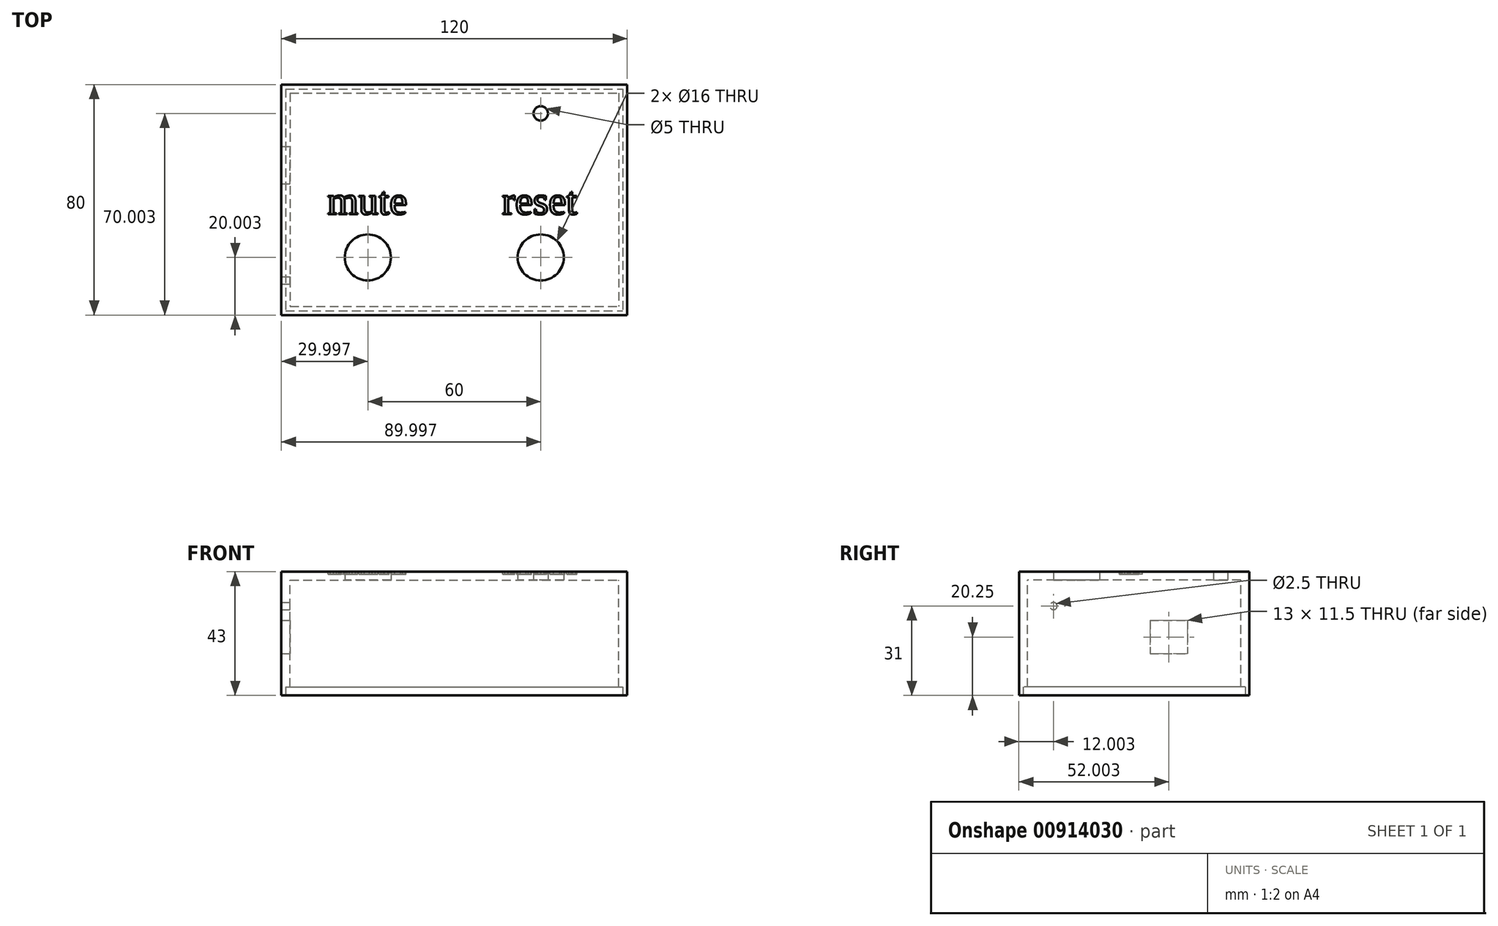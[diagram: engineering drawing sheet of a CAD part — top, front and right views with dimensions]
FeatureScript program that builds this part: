
annotation { "Feature Type Name" : "Feature", "Feature Type Description" : "" }
export const myFeature = defineFeature(function(context is Context, id is Id, definition is map)
    precondition{}
    {
        {
            var Q0;
            Q0=qCreatedBy(makeId("Top.planeOp"),FACE);
            var sketch = newSketch(context, id + "F0", { "sketchPlane" : qUnion([Q0])});
            skLineSegment(sketch, "E0.bottom", {"start": v(-70.32, 62.2) * mm, "end": v(49.68, 62.2) * mm});
            skLineSegment(sketch, "E0.top", {"start": v(-70.32, -17.8) * mm, "end": v(49.68, -17.8) * mm});
            skLineSegment(sketch, "E0.left", {"start": v(-70.32, 62.2) * mm, "end": v(-70.32, -17.8) * mm});
            skLineSegment(sketch, "E0.right", {"start": v(49.68, 62.2) * mm, "end": v(49.68, -17.8) * mm});
            skLineSegment(sketch, "E1", {"start": v(-10.32, 62.2) * mm, "end": v(-10.32, -17.8) * mm});
            skLineSegment(sketch, "E2", {"start": v(-70.32, 22.2) * mm, "end": v(49.68, 22.2) * mm});
            skLineSegment(sketch, "E3", {"start": v(19.68, 62.2) * mm, "end": v(19.68, -17.8) * mm});
            skLineSegment(sketch, "E4", {"start": v(-40.32, 62.2) * mm, "end": v(-40.32, -17.8) * mm});
            skLineSegment(sketch, "E5", {"start": v(-70.32, 52.2) * mm, "end": v(49.68, 52.2) * mm});
            skLineSegment(sketch, "E6", {"start": v(49.68, 2.2) * mm, "end": v(-70.32, 2.2) * mm});
            skCircle(sketch, "E7", {"center": v(19.68, 52.2) * mm, "radius": 2.5 * mm});
            skCircle(sketch, "E8", {"center": v(19.68, 2.2) * mm, "radius": 8 * mm});
            skCircle(sketch, "E9", {"center": v(-40.32, 2.2) * mm, "radius": 8 * mm});
            skSolve(sketch);
        }
        {
            var Q0;
            Q0 = qSketchRegion(id + "F0", true);
            var Q1;
            {var subQ0=sQuery(id+"F0.wireOp",EDGE,"E5");var subQ1=sQuery(id+"F0.wireOp",EDGE,"E1");var subQ2=makeQuery(id+"F0.imprint","INTERSECT",VERTEX,{"derivedFrom":[subQ1,subQ0]});Q1=makeQuery(id+"F0.imprint","IMPRINT",FACE,{"disambiguationData":[TD([[makeQuery(id+"F0.imprint","IMPRINT",EDGE,{"disambiguationData":[TD([[subQ2,-1.0]])],"derivedFrom":subQ1}),-1.0]])]});}
            var Q2;
            {var subQ0=sQuery(id+"F0.wireOp",EDGE,"E5");var subQ1=sQuery(id+"F0.wireOp",EDGE,"E1");var subQ2=makeQuery(id+"F0.imprint","INTERSECT",VERTEX,{"derivedFrom":[subQ1,subQ0]});Q2=makeQuery(id+"F0.imprint","IMPRINT",FACE,{"disambiguationData":[TD([[makeQuery(id+"F0.imprint","IMPRINT",EDGE,{"disambiguationData":[TD([[subQ2,-1.0]])],"derivedFrom":subQ1}),1.0]])]});}
            var Q3;
            {var subQ1=sQuery(id+"F0.wireOp",EDGE,"E1");var subQ5=sQuery(id+"F0.wireOp",EDGE,"E2");var subQ6=makeQuery(id+"F0.imprint","INTERSECT",VERTEX,{"derivedFrom":[subQ1,subQ5]});Q3=makeQuery(id+"F0.imprint","IMPRINT",FACE,{"disambiguationData":[TD([[makeQuery(id+"F0.imprint","IMPRINT",EDGE,{"disambiguationData":[TD([[subQ6,-1.0]])],"derivedFrom":subQ1}),1.0]])]});}
            var Q4;
            {var subQ1=sQuery(id+"F0.wireOp",EDGE,"E2");var subQ5=sQuery(id+"F0.wireOp",EDGE,"E1");var subQ6=makeQuery(id+"F0.imprint","INTERSECT",VERTEX,{"derivedFrom":[subQ5,subQ1]});Q4=makeQuery(id+"F0.imprint","IMPRINT",FACE,{"disambiguationData":[TD([[makeQuery(id+"F0.imprint","IMPRINT",EDGE,{"disambiguationData":[TD([[subQ6,-1.0]])],"derivedFrom":subQ5}),-1.0]])]});}
            extrude(context, id + "F1", {"entities" : qUnion([Q0, Q1, Q2, Q3, Q4]), "depth" : 3 * mm, "offsetDistance" : 25 * mm});
        }
        {
            var Q0;
            {var subQ1=sQuery(id+"F0.wireOp",EDGE,"E0.top");var subQ5=sQuery(id+"F0.wireOp",EDGE,"E0.left");var subQ6=makeQuery(id+"F0.imprint","INTERSECT",VERTEX,{"derivedFrom":[subQ1,subQ5]});Q0=makeQuery(id+"F0.imprint","IMPRINT",FACE,{"disambiguationData":[TD([[makeQuery(id+"F0.imprint","IMPRINT",EDGE,{"disambiguationData":[TD([[subQ6,-1.0]])],"derivedFrom":subQ1}),1.0]])]});}
            var sketch = newSketch(context, id + "F2", { "sketchPlane" : qUnion([Q0])});
            skLineSegment(sketch, "E10.0", {"start": v(-67.32, -14.8) * mm, "end": v(46.68, -14.8) * mm});
            skLineSegment(sketch, "E10.1", {"start": v(-67.32, 59.2) * mm, "end": v(-67.32, -14.8) * mm});
            skLineSegment(sketch, "E10.2", {"start": v(-67.32, 59.2) * mm, "end": v(46.68, 59.2) * mm});
            skLineSegment(sketch, "E10.3", {"start": v(46.68, 59.2) * mm, "end": v(46.68, -14.8) * mm});
            skLineSegment(sketch, "E11.0", {"start": v(-70.32, -17.8) * mm, "end": v(49.68, -17.8) * mm});
            skLineSegment(sketch, "E11.1", {"start": v(-70.32, 62.2) * mm, "end": v(-70.32, -17.8) * mm});
            skLineSegment(sketch, "E11.2", {"start": v(-70.32, 62.2) * mm, "end": v(49.68, 62.2) * mm});
            skLineSegment(sketch, "E11.3", {"start": v(49.68, 62.2) * mm, "end": v(49.68, -17.8) * mm});
            skSolve(sketch);
        }
        {
            var Q0;
            {var subQ10=sQuery(id+"F2.wireOp",EDGE,"E10.1");var subQ11=sQuery(id+"F2.wireOp",EDGE,"E10.0");var subQ12=makeQuery(id+"F2.imprint","INTERSECT",VERTEX,{"derivedFrom":[subQ11,subQ10]});Q0=makeQuery(id+"F2.imprint","IMPRINT",FACE,{"disambiguationData":[TD([[makeQuery(id+"F2.imprint","IMPRINT",EDGE,{"disambiguationData":[TD([[subQ12,-1.0]])],"derivedFrom":subQ11}),-1.0]])]});}
            var Q1;
            {var subQ1=sQuery(id+"F2.wireOp",EDGE,"E10.2");Q1=makeQuery(id+"F2.imprint","IMPRINT",FACE,{"disambiguationData":[TD([[makeQuery(id+"F2.imprint","IMPRINT",EDGE,{"derivedFrom":subQ1}),1.0]])]});}
            extrude(context, id + "F3", {"entities" : qUnion([Q0, Q1]), "operationType" : NewBodyOperationType.ADD, "oppositeDirection" : true, "depth" : 40 * mm, "offsetDistance" : 25 * mm});
        }
        {
            var Q0;
            Q0=makeQuery(id+"F3.opExtrude","CAP_FACE",FACE,{"disambiguationData":[OSD([sQuery(id+"F2.wireOp",EDGE,"E10.0"),sQuery(id+"F2.wireOp",EDGE,"E10.1"),sQuery(id+"F2.wireOp",EDGE,"E10.2"),sQuery(id+"F2.wireOp",EDGE,"E10.3"),sQuery(id+"F2.wireOp",EDGE,"E11.0"),sQuery(id+"F2.wireOp",EDGE,"E11.1"),sQuery(id+"F2.wireOp",EDGE,"E11.2"),sQuery(id+"F2.wireOp",EDGE,"E11.3")])],"isStart":false});
            var sketch = newSketch(context, id + "F4", { "sketchPlane" : qUnion([Q0])});
            skLineSegment(sketch, "E12.0", {"start": v(-68.82, 16.3) * mm, "end": v(48.18, 16.3) * mm});
            skLineSegment(sketch, "E12.1", {"start": v(-68.82, -60.7) * mm, "end": v(-68.82, 16.3) * mm});
            skLineSegment(sketch, "E12.2", {"start": v(-68.82, -60.7) * mm, "end": v(48.18, -60.7) * mm});
            skLineSegment(sketch, "E12.3", {"start": v(48.18, -60.7) * mm, "end": v(48.18, 16.3) * mm});
            skSolve(sketch);
        }
        {
            var Q0;
            Q0=makeQuery(id+"F4.imprint","IMPRINT",FACE,{"disambiguationData":[TD([[makeQuery(id+"F4.imprint","IMPRINT",EDGE,{"derivedFrom":sQuery(id+"F4.wireOp",EDGE,"E12.0")}),-1.0]])]});
            extrude(context, id + "F5", {"entities" : qUnion([Q0]), "operationType" : NewBodyOperationType.REMOVE, "oppositeDirection" : true, "depth" : 3 * mm, "offsetDistance" : 25 * mm});
        }
        {
            var Q0;
            Q0=makeQuery(id+"F3.opExtrude","SWEPT_FACE",FACE,{"disambiguationData":[OSD([sQuery(id+"F2.wireOp",EDGE,"E10.1")])]});
            var sketch = newSketch(context, id + "F6", { "sketchPlane" : qUnion([Q0])});
            skLineSegment(sketch, "E13.bottom", {"start": v(27.7, -14) * mm, "end": v(40.7, -14) * mm});
            skLineSegment(sketch, "E13.top", {"start": v(27.7, -25.5) * mm, "end": v(40.7, -25.5) * mm});
            skLineSegment(sketch, "E13.left", {"start": v(27.7, -14) * mm, "end": v(27.7, -25.5) * mm});
            skLineSegment(sketch, "E13.right", {"start": v(40.7, -14) * mm, "end": v(40.7, -25.5) * mm});
            skCircle(sketch, "E14", {"center": v(-5.8, -9) * mm, "radius": 1.25 * mm});
            skCircle(sketch, "E15", {"center": v(-5.8, -9) * mm, "radius": 8 * mm});
            skSolve(sketch);
        }
        {
            var Q0;
            Q0=makeQuery(id+"F6.imprint","IMPRINT",FACE,{"disambiguationData":[TD([[makeQuery(id+"F6.imprint","IMPRINT",EDGE,{"derivedFrom":sQuery(id+"F6.wireOp",EDGE,"E13.bottom")}),-1.0]])]});
            var Q1;
            Q1=makeQuery(id+"F6.imprint","IMPRINT",FACE,{"disambiguationData":[TD([[makeQuery(id+"F6.imprint","IMPRINT",EDGE,{"derivedFrom":sQuery(id+"F6.wireOp",EDGE,"E14")}),1.0]])]});
            extrude(context, id + "F7", {"entities" : qUnion([Q0, Q1]), "operationType" : NewBodyOperationType.REMOVE, "oppositeDirection" : true, "depth" : 25 * mm, "offsetDistance" : 25 * mm});
        }
        {
            var Q0;
            Q0=makeQuery(id+"F1.opExtrude","CAP_FACE",FACE,{"disambiguationData":[OSD([sQuery(id+"F0.wireOp",EDGE,"E0.bottom"),sQuery(id+"F0.wireOp",EDGE,"E0.top"),sQuery(id+"F0.wireOp",EDGE,"E0.left"),sQuery(id+"F0.wireOp",EDGE,"E0.right"),sQuery(id+"F0.wireOp",EDGE,"E7"),sQuery(id+"F0.wireOp",EDGE,"E8"),sQuery(id+"F0.wireOp",EDGE,"E9")])],"isStart":false});
            var sketch = newSketch(context, id + "F8", { "sketchPlane" : qUnion([Q0])});
            skText(sketch, "E16", { "text": "mute", "fontName": "Tinos-Regular.ttf"});
            skText(sketch, "E17", { "text": "reset", "fontName": "Tinos-Regular.ttf"});
            const initialGuessF8  = {"E16": [-0.0544, 0.0172, 1, 0, 0.01], "E17": [0.00617, 0.0172, 1, 0, 0.01]};
            skSetInitialGuess(sketch, initialGuessF8);
            skSolve(sketch);
        }
        {
            var Q0;
            Q0 = qSketchRegion(id + "F8", true);
            extrude(context, id + "F9", {"entities" : qUnion([Q0]), "operationType" : NewBodyOperationType.REMOVE, "oppositeDirection" : true, "depth" : 1 * mm, "offsetDistance" : 25 * mm});
        }
    });
